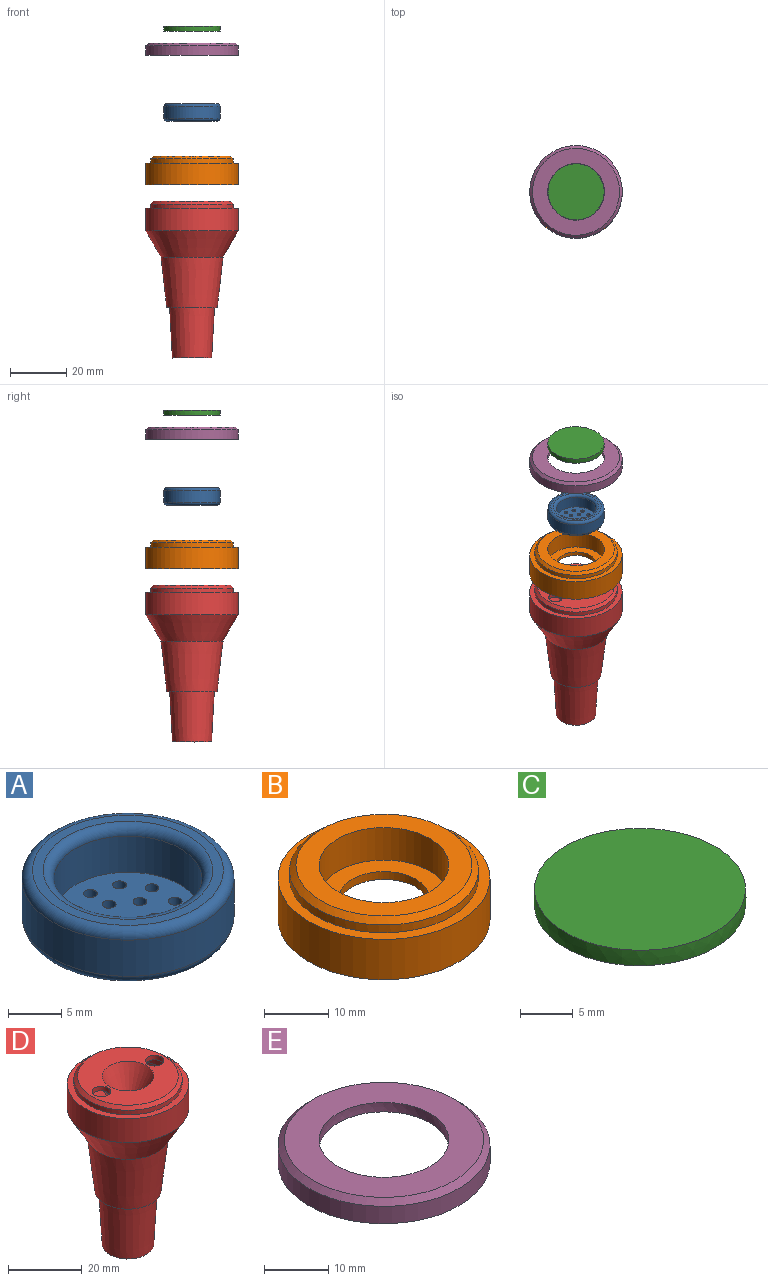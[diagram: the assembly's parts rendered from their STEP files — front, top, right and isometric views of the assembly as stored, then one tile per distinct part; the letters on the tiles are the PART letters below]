
ASSEMBLY  parts=5 mates=4
PART A: 23 faces, bbox 21.6x21.6x6.2 mm
  f0: plane 18x18mm, normal (0,0,-1), area 234.6mm2, adj f1,f8,f9,f10,f11,f12,f13,f14
  f1: torus R=9mm, axis (0,0,-1), area 95.1mm2, adj f0,f2
  f2: cylinder r=10mm len=20mm, axis (0,0,-1), area 262.6mm2, adj f1,f3
  f3: torus R=9mm, axis (0,0,-1), area 95.1mm2, adj f2,f4
  f4: plane 18x18mm, normal (0,0,1), area 53.4mm2, adj f3,f5
  f5: torus R=8mm, axis (0,0,-1), area 72.7mm2, adj f4,f6
  f6: cylinder r=7mm len=14mm, axis (0,0,-1), area 183.8mm2, adj f5,f7
  f7: plane 14x14mm, normal (0,0,1), area 134mm2, adj f6,f8,f9,f10,f11,f12,f13,f14
  f8: cylinder r=0.65mm len=1.3mm, axis (0,0,1), area 4.1mm2, adj f0,f7
  f9: cylinder r=0.65mm len=1.3mm, axis (0,0,1), area 4.1mm2, adj f0,f7
  f10: cylinder r=0.65mm len=1.3mm, axis (0,0,1), area 4.1mm2, adj f0,f7
  f11: cylinder r=0.65mm len=1.3mm, axis (0,0,1), area 4.1mm2, adj f0,f7
  f12: cylinder r=0.65mm len=1.3mm, axis (0,0,1), area 4.1mm2, adj f0,f7
  f13: cylinder r=0.65mm len=1.3mm, axis (0,0,1), area 4.1mm2, adj f0,f7
  f14: cylinder r=0.65mm len=1.3mm, axis (0,0,1), area 4.1mm2, adj f0,f7
  f15: cylinder r=0.65mm len=1.3mm, axis (0,0,1), area 4.1mm2, adj f0,f7
  f16: cylinder r=0.65mm len=1.3mm, axis (0,0,1), area 4.1mm2, adj f0,f7
  f17: cylinder r=0.65mm len=1.3mm, axis (0,0,1), area 4.1mm2, adj f0,f7
  f18: cylinder r=0.65mm len=1.3mm, axis (0,0,1), area 4.1mm2, adj f0,f7
  f19: cylinder r=0.65mm len=1.3mm, axis (0,0,1), area 4.1mm2, adj f0,f7
  f20: cylinder r=0.65mm len=1.3mm, axis (0,0,1), area 4.1mm2, adj f0,f7
  f21: cylinder r=0.65mm len=1.3mm, axis (0,0,1), area 4.1mm2, adj f0,f7
  f22: cylinder r=0.65mm len=1.3mm, axis (0,0,1), area 4.1mm2, adj f0,f7
PART B: 12 faces, bbox 33x33x10.2 mm
  f0: plane 27.4x27.4mm, normal (0,0,-1), area 435.7mm2, adj f9,f10
  f1: cylinder r=14.7mm len=29.4mm, axis (0,0,-1), area 138.5mm2, adj f2,f10
  f2: plane 33x33mm, normal (0,0,-1), area 176.4mm2, adj f1,f3
  f3: cylinder r=16.5mm len=33mm, axis (0,0,-1), area 796.2mm2, adj f2,f4
  f4: plane 33x33mm, normal (0,0,1), area 176.4mm2, adj f3,f5
  f5: cylinder r=14.7mm len=29.4mm, axis (0,0,-1), area 138.5mm2, adj f4,f11
  f6: plane 27.4x27.4mm, normal (0,0,1), area 269.2mm2, adj f7,f11
  f7: cylinder r=10.1mm len=20.2mm, axis (0,0,-1), area 392.2mm2, adj f6,f8
  f8: plane 20.2x20.2mm, normal (0,0,1), area 166.5mm2, adj f7,f9
  f9: cylinder r=7mm len=14mm, axis (0,0,-1), area 66mm2, adj f0,f8
  f10: cone r=13.7mm half-angle=45deg, axis (0,0,-1), area 126.2mm2, adj f0,f1
  f11: cone r=14.7mm half-angle=45deg, axis (0,0,-1), area 126.2mm2, adj f5,f6
PART C: 3 faces, bbox 20.1x20.1x1.8 mm
  f0: plane 20x20mm, normal (0,0,1), area 314.2mm2, adj f2
  f1: plane 20x20mm, normal (0,0,-1), area 314.2mm2, adj f2
  f2: sphere r=10.04mm, area 113.6mm2, adj f0,f1
PART D: 25 faces, bbox 33x33x55.9 mm
  f0: cone r=3mm half-angle=27.6deg, axis (0,0,1), area 361.7mm2, adj f2,f3,f11,f12
  f1: plane 11.16x11.16mm, normal (0,0,1), area 69.6mm2, adj f2,f10
  f2: cylinder r=3mm len=43.52mm, axis (0,0,-1), area 820.4mm2, adj f0,f1
  f3: plane 26.4x26.4mm, normal (0,0,-1), area 312mm2, adj f0,f4,f11,f12
  f4: cylinder r=13.2mm len=26.4mm, axis (0,0,-1), area 207.3mm2, adj f3,f5
  f5: plane 30x30mm, normal (0,0,-1), area 159.5mm2, adj f4,f6
  f6: cylinder r=15mm len=30mm, axis (0,0,-1), area 574.6mm2, adj f5,f7
  f7: cone r=15mm half-angle=30.1deg, axis (0,0,1), area 831.9mm2, adj f6,f8
  f8: cone r=7.66mm half-angle=6.5deg, axis (0,0,1), area 927.1mm2, adj f7,f9
  f9: plane 15.32x15.32mm, normal (0,0,1), area 48.4mm2, adj f8,f10
  f10: cone r=5.58mm half-angle=3.2deg, axis (0,0,1), area 688.8mm2, adj f1,f9
  f11: cylinder r=2.5mm len=5mm, axis (0,0,1), area 23.9mm2, adj f0,f3,f23
  f12: cylinder r=2.5mm len=5mm, axis (0,0,1), area 23.9mm2, adj f0,f3,f23
  f13: cone r=1.5mm half-angle=27.6deg, axis (0,0,1), area 316.5mm2, adj f14,f23
  f14: cylinder r=1.5mm len=45.39mm, axis (0,0,-1), area 427.8mm2, adj f13,f15
  f15: plane 14x14mm, normal (0,0,-1), area 146.9mm2, adj f14,f16
  f16: cone r=7mm half-angle=3.2deg, axis (0,0,1), area 849.5mm2, adj f15,f17
  f17: plane 18x18mm, normal (0,0,-1), area 53.4mm2, adj f16,f18
  f18: cone r=9mm half-angle=6.5deg, axis (0,0,1), area 1141.7mm2, adj f17,f19
  f19: cone r=16.5mm half-angle=30.1deg, axis (0,0,1), area 939.6mm2, adj f18,f20
  f20: cylinder r=16.5mm len=33mm, axis (0,0,-1), area 829.4mm2, adj f19,f21
  f21: plane 33x33mm, normal (0,0,1), area 176.4mm2, adj f20,f22
  f22: cylinder r=14.7mm len=29.4mm, axis (0,0,-1), area 138.5mm2, adj f21,f24
  f23: plane 27.4x27.4mm, normal (0,0,1), area 396.4mm2, adj f11,f12,f13,f24
  f24: cone r=14.7mm half-angle=45deg, axis (0,0,-1), area 126.2mm2, adj f22,f23
PART E: 8 faces, bbox 33x33x4.3 mm
  f0: cylinder r=16.5mm len=33mm, axis (0,0,-1), area 342.1mm2, adj f5,f6
  f1: plane 31x31mm, normal (0,0,1), area 434.3mm2, adj f2,f6
  f2: sphere r=10.14mm, area 114.7mm2, adj f1,f3
  f3: plane 29.4x29.4mm, normal (0,0,-1), area 358.4mm2, adj f2,f4
  f4: cylinder r=14.7mm len=29.4mm, axis (0,0,-1), area 138.5mm2, adj f3,f7
  f5: plane 33x33mm, normal (0,0,-1), area 80.9mm2, adj f0,f7
  f6: cone r=16.5mm half-angle=45deg, axis (0,0,-1), area 142.2mm2, adj f0,f1
  f7: cone r=14.7mm half-angle=45deg, axis (0,0,-1), area 135.1mm2, adj f4,f5
PLACE A t=(0.9,0.33,-20.73)mm
PLACE B t=(0.9,0.33,-37.5)mm
PLACE C t=(0.9,0.33,-1.58)mm
PLACE D t=(0.9,0.33,-27.62)mm
PLACE E t=(0.9,0.33,-7.67)mm
MATE slider A.f1 <-> B.f1  axis (0,0,-1) through (0.9,0.33,14.54)mm
MATE cylindrical C.f2 <-> E.f0  axis (0,0,1) through (0.9,0.33,44.45)mm
MATE slider D.f0 <-> B.f1  axis (0,0,-1) through (0.9,0.33,-18.87)mm
MATE slider E.f0 <-> B.f1  axis (0,0,-1) through (0.9,0.33,36.7)mm
